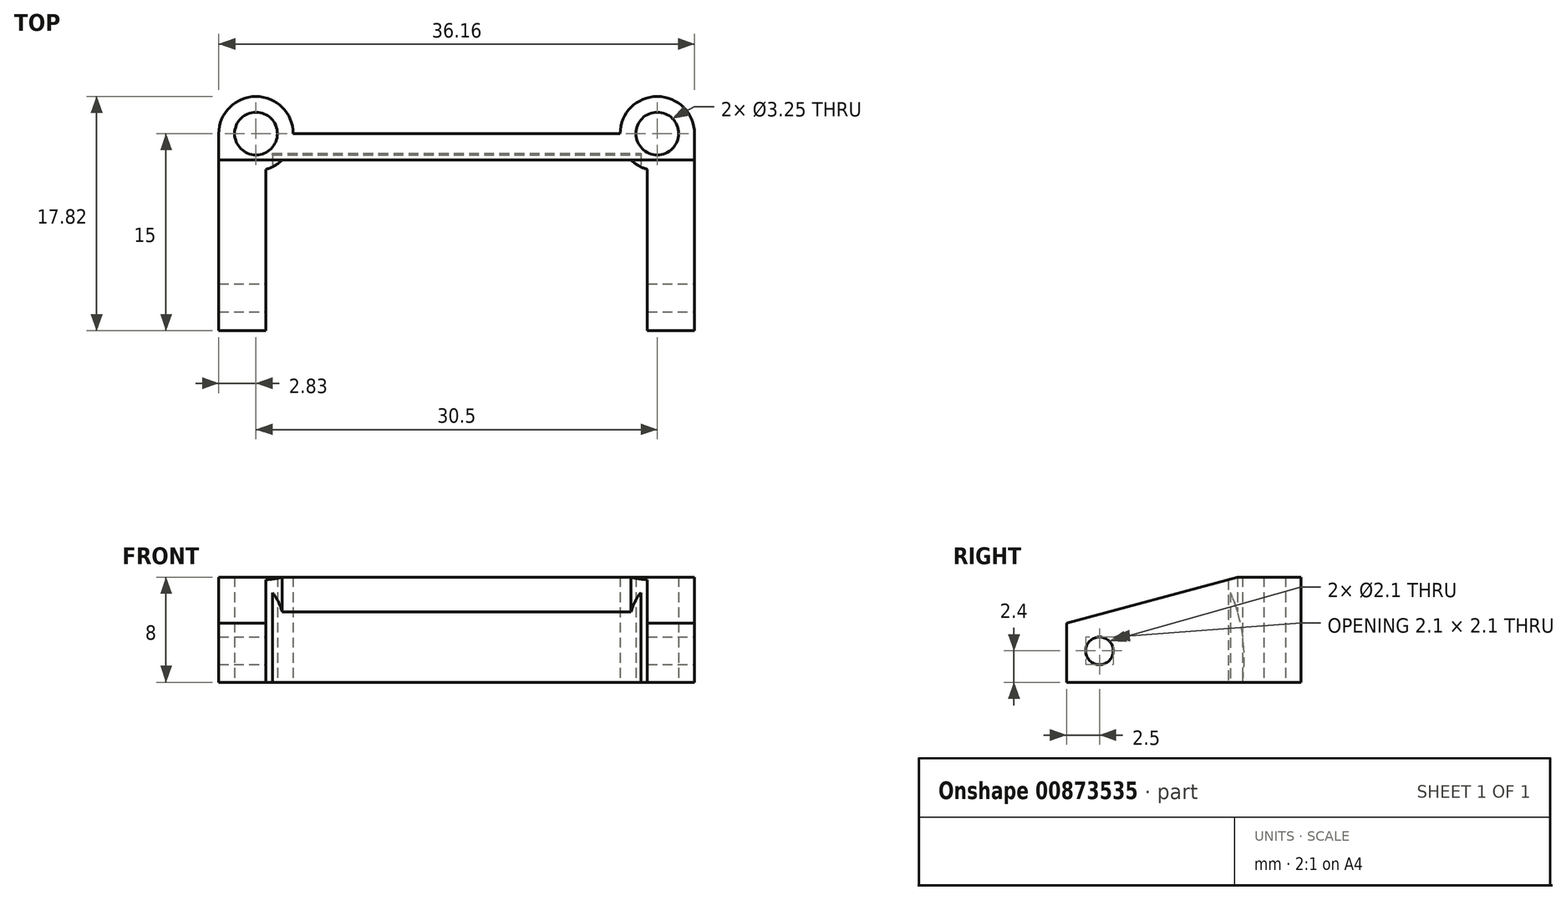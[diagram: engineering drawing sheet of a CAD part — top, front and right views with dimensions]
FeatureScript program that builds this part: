
annotation { "Feature Type Name" : "Feature", "Feature Type Description" : "" }
export const myFeature = defineFeature(function(context is Context, id is Id, definition is map)
    precondition{}
    {
        {
            var Q0;
            Q0=qCreatedBy(makeId("Top.planeOp"),FACE);
            var sketch = newSketch(context, id + "F0", { "sketchPlane" : qUnion([Q0])});
            skCircle(sketch, "E0", {"center": v(15.25, 0) * mm, "radius": 1.63 * mm});
            skLineSegment(sketch, "E1.top", {"start": v(18.07, -15) * mm, "end": v(12.97, -15) * mm});
            skCircle(sketch, "E2", {"center": v(15.25, 0) * mm, "radius": 2.83 * mm});
            skLineSegment(sketch, "E3", {"start": v(0, 0) * mm, "end": v(12.42, 0) * mm});
            skLineSegment(sketch, "E4", {"start": v(14.5, -15) * mm, "end": v(14.5, -2.72) * mm});
            skPoint(sketch, "E5.visualSharp", {"position": v(14.5, -2.72) * mm});
            skLineSegment(sketch, "E6.MirrorCS", {"start": v(-18.07, -15) * mm, "end": v(-12.97, -15) * mm});
            skLineSegment(sketch, "E7.MirrorCS", {"start": v(0, 0) * mm, "end": v(-12.42, 0) * mm});
            skPoint(sketch, "E8.MirrorP", {"position": v(-14.5, -2.72) * mm});
            skLineSegment(sketch, "E9.MirrorCS", {"start": v(-14.5, -15) * mm, "end": v(-14.5, -2.72) * mm});
            skCircle(sketch, "E10.MirrorC", {"center": v(-15.25, 0) * mm, "radius": 1.63 * mm});
            skCircle(sketch, "E11.MirrorC", {"center": v(-15.25, 0) * mm, "radius": 2.83 * mm});
            skLineSegment(sketch, "E12", {"start": v(0, -2) * mm, "end": v(13.25, -2) * mm});
            skLineSegment(sketch, "E13.MirrorCS", {"start": v(0, -2) * mm, "end": v(-13.25, -2) * mm});
            skLineSegment(sketch, "E14", {"start": v(18.07, 0) * mm, "end": v(18.07, -15) * mm});
            skLineSegment(sketch, "E15.MirrorCS", {"start": v(-18.07, 0) * mm, "end": v(-18.07, -15) * mm});
            skSolve(sketch);
        }
        {
            var Q0;
            Q0 = qSketchRegion(id + "F0", true);
            extrude(context, id + "F1", {"entities" : qUnion([Q0]), "depth" : 8 * mm, "offsetDistance" : 25 * mm});
        }
        {
            var Q0;
            Q0=makeQuery(id+"F1.opExtrude","CAP_FACE",FACE,{"disambiguationData":[OSD([sQuery(id+"F0.wireOp",EDGE,"E0"),sQuery(id+"F0.wireOp",EDGE,"E1.top"),sQuery(id+"F0.wireOp",EDGE,"E1.left"),sQuery(id+"F0.wireOp",EDGE,"E2"),sQuery(id+"F0.wireOp",EDGE,"E3"),sQuery(id+"F0.wireOp",EDGE,"E4"),sQuery(id+"F0.wireOp",EDGE,"E6.MirrorCS"),sQuery(id+"F0.wireOp",EDGE,"505e8006-f65f-411e-bb6e-7c7b75ca80f43.MirrorCS"),sQuery(id+"F0.wireOp",EDGE,"E7.MirrorCS"),sQuery(id+"F0.wireOp",EDGE,"E9.MirrorCS"),sQuery(id+"F0.wireOp",EDGE,"E10.MirrorC"),sQuery(id+"F0.wireOp",EDGE,"E11.MirrorC"),sQuery(id+"F0.wireOp",EDGE,"E12"),sQuery(id+"F0.wireOp",EDGE,"E13.MirrorCS")])],"isStart":true});
            var sketch = newSketch(context, id + "F2", { "sketchPlane" : qUnion([Q0])});
            skLineSegment(sketch, "E16.bottom", {"start": v(14.5, 15) * mm, "end": v(18.07, 15) * mm});
            skLineSegment(sketch, "E16.top", {"start": v(14.5, 3.45) * mm, "end": v(18.07, 3.45) * mm});
            skLineSegment(sketch, "E16.left", {"start": v(14.5, 15) * mm, "end": v(14.5, 3.45) * mm});
            skLineSegment(sketch, "E16.right", {"start": v(18.07, 15) * mm, "end": v(18.07, 3.45) * mm});
            skLineSegment(sketch, "E17.MirrorCS", {"start": v(-14.5, 15) * mm, "end": v(-14.5, 3.45) * mm});
            skLineSegment(sketch, "E18.MirrorCS", {"start": v(-14.5, 15) * mm, "end": v(-18.07, 15) * mm});
            skLineSegment(sketch, "E19.MirrorCS", {"start": v(-14.5, 3.45) * mm, "end": v(-18.07, 3.45) * mm});
            skLineSegment(sketch, "E20.MirrorCS", {"start": v(-18.07, 15) * mm, "end": v(-18.07, 3.45) * mm});
            skSolve(sketch);
        }
        {
            var Q0;
            Q0=qCreatedBy(makeId("Right.planeOp"),FACE);
            var sketch = newSketch(context, id + "F3", { "sketchPlane" : qUnion([Q0])});
            skCircle(sketch, "E21", {"center": v(-12.5, 2.4) * mm, "radius": 1.05 * mm});
            skLineSegment(sketch, "E22", {"start": v(-15, 0) * mm, "end": v(-15, 4.5) * mm});
            skLineSegment(sketch, "E23", {"start": v(-15, 4.5) * mm, "end": v(-2, 8) * mm});
            skLineSegment(sketch, "E24", {"start": v(-2, 8) * mm, "end": v(-15, 8) * mm});
            skLineSegment(sketch, "E25", {"start": v(-15, 8) * mm, "end": v(-15, 4.5) * mm});
            skLineSegment(sketch, "E26", {"start": v(-15, 0) * mm, "end": v(-15, -1.5) * mm});
            skSolve(sketch);
        }
        {
            var Q0;
            Q0 = qSketchRegion(id + "F3", true);
            extrude(context, id + "F4", {"entities" : qUnion([Q0]), "operationType" : NewBodyOperationType.REMOVE, "endBound" : BoundingType.THROUGH_ALL, "oppositeDirection" : true, "depth" : 25 * mm, "offsetDistance" : 25 * mm, "hasSecondDirection" : true, "secondDirectionBound" : SecondDirectionBoundingType.THROUGH_ALL, "secondDirectionOppositeDirection" : false, "secondDirectionDepth" : 25 * mm});
        }
        {
            var Q0;
            Q0=qCreatedBy(makeId("Right.planeOp"),FACE);
            var sketch = newSketch(context, id + "F5", { "sketchPlane" : qUnion([Q0])});
            skLineSegment(sketch, "E27", {"start": v(0, 8) * mm, "end": v(-2, 8) * mm});
            skLineSegment(sketch, "E28", {"start": v(-2, 8) * mm, "end": v(0, 9.41) * mm});
            skLineSegment(sketch, "E29", {"start": v(0, 9.41) * mm, "end": v(0, 8) * mm});
            skSolve(sketch);
        }
        {
            var Q0;
            Q0=qCreatedBy(makeId("Top.planeOp"),FACE);
            cPlane(context, id + "F6", {"entities" : qUnion([Q0]), "cplaneType" : CPlaneType.OFFSET, "offset" : 1.85 * mm, "width" : 150 * mm, "height" : 150 * mm});
        }
        {
            var Q0;
            Q0=qCreatedBy(id+"F6.planeOp",FACE);
            var sketch = newSketch(context, id + "F7", { "sketchPlane" : qUnion([Q0])});
            skLineSegment(sketch, "E30", {"start": v(0, -1.5) * mm, "end": v(14, -1.5) * mm});
            skLineSegment(sketch, "E31", {"start": v(14, -1.5) * mm, "end": v(14, -4.72) * mm});
            skLineSegment(sketch, "E32", {"start": v(14, -4.72) * mm, "end": v(0, -4.72) * mm});
            skLineSegment(sketch, "E33.MirrorCS", {"start": v(-14, -1.5) * mm, "end": v(-14, -4.72) * mm});
            skLineSegment(sketch, "E34.MirrorCS", {"start": v(0, -1.5) * mm, "end": v(-14, -1.5) * mm});
            skLineSegment(sketch, "E35.MirrorCS", {"start": v(-14, -4.72) * mm, "end": v(0, -4.72) * mm});
            skLineSegment(sketch, "E36", {"start": v(0, -14) * mm, "end": v(7, -14) * mm});
            skSolve(sketch);
        }
        {
            var Q0;
            Q0 = qSketchRegion(id + "F7", true);
            var Q1;
            Q1=sQuery(id+"F7.wireOp",EDGE,"E36");
            revolve(context, id + "F8", {"operationType" : NewBodyOperationType.REMOVE, "surfaceOperationType" : NewSurfaceOperationType.NEW, "entities" : qUnion([Q0]), "axis" : qUnion([Q1]), "revolveType" : RevolveType.FULL, "oppositeDirection" : true});
        }
    });
